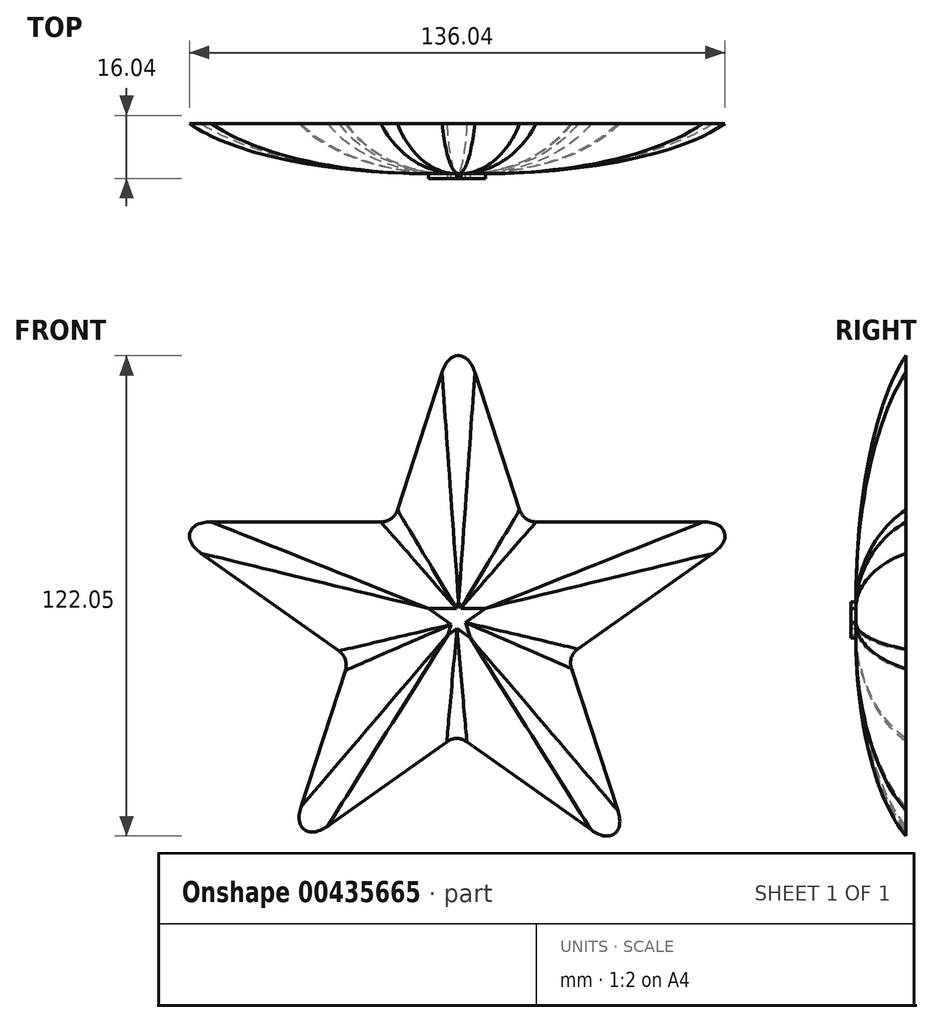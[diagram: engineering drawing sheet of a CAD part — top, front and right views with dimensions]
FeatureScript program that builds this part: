
annotation { "Feature Type Name" : "Feature", "Feature Type Description" : "" }
export const myFeature = defineFeature(function(context is Context, id is Id, definition is map)
    precondition{}
    {
        {
            var Q0;
            Q0=qCreatedBy(makeId("Front.planeOp"),FACE);
            var sketch = newSketch(context, id + "F0", { "sketchPlane" : qUnion([Q0])});
            skLineSegment(sketch, "E0", {"start": v(-44.05, -76) * mm, "end": v(76, 8.97) * mm});
            skLineSegment(sketch, "E1", {"start": v(76, 8.97) * mm, "end": v(-76.57, 8.97) * mm});
            skLineSegment(sketch, "E2", {"start": v(-76.57, 8.97) * mm, "end": v(43.16, -76) * mm});
            skLineSegment(sketch, "E3", {"start": v(44.3, -76) * mm, "end": v(0, 59.77) * mm});
            skLineSegment(sketch, "E4", {"start": v(0, 59.77) * mm, "end": v(-44.05, -76) * mm});
            skLineSegment(sketch, "E5", {"start": v(43.16, -76) * mm, "end": v(44.3, -76) * mm});
            skSolve(sketch);
        }
        {
            var Q0;
            {var subQ0=sQuery(id+"F0.wireOp",EDGE,"E3");var subQ1=sQuery(id+"F0.wireOp",EDGE,"E1");var subQ2=makeQuery(id+"F0.imprint","INTERSECT",VERTEX,{"derivedFrom":[subQ1,subQ0]});Q0=makeQuery(id+"F0.imprint","IMPRINT",FACE,{"disambiguationData":[TD([[makeQuery(id+"F0.imprint","IMPRINT",EDGE,{"disambiguationData":[TD([[subQ2,-1.0]])],"derivedFrom":subQ1}),-1.0]])]});}
            var Q1;
            {var subQ0=sQuery(id+"F0.wireOp",EDGE,"E2");var subQ1=sQuery(id+"F0.wireOp",EDGE,"E1");var subQ2=makeQuery(id+"F0.imprint","INTERSECT",VERTEX,{"derivedFrom":[subQ1,subQ0]});Q1=makeQuery(id+"F0.imprint","IMPRINT",FACE,{"disambiguationData":[TD([[makeQuery(id+"F0.imprint","IMPRINT",EDGE,{"disambiguationData":[TD([[subQ2,1.0]])],"derivedFrom":subQ1}),1.0]])]});}
            var Q2;
            {var subQ0=sQuery(id+"F0.wireOp",EDGE,"E4");var subQ1=sQuery(id+"F0.wireOp",EDGE,"E0");var subQ2=makeQuery(id+"F0.imprint","INTERSECT",VERTEX,{"derivedFrom":[subQ1,subQ0]});Q2=makeQuery(id+"F0.imprint","IMPRINT",FACE,{"disambiguationData":[TD([[makeQuery(id+"F0.imprint","IMPRINT",EDGE,{"disambiguationData":[TD([[subQ2,-1.0]])],"derivedFrom":subQ1}),1.0]])]});}
            var Q3;
            {var subQ0=sQuery(id+"F0.wireOp",EDGE,"E1");var subQ1=sQuery(id+"F0.wireOp",EDGE,"E0");var subQ2=makeQuery(id+"F0.imprint","INTERSECT",VERTEX,{"derivedFrom":[subQ1,subQ0]});Q3=makeQuery(id+"F0.imprint","IMPRINT",FACE,{"disambiguationData":[TD([[makeQuery(id+"F0.imprint","IMPRINT",EDGE,{"disambiguationData":[TD([[subQ2,1.0]])],"derivedFrom":subQ1}),1.0]])]});}
            var Q4;
            {var subQ5=sQuery(id+"F0.wireOp",EDGE,"E5");Q4=makeQuery(id+"F0.imprint","IMPRINT",FACE,{"disambiguationData":[TD([[makeQuery(id+"F0.imprint","IMPRINT",EDGE,{"derivedFrom":subQ5}),1.0]])]});}
            var Q5;
            {var subQ1=sQuery(id+"F0.wireOp",EDGE,"E0");var subQ5=sQuery(id+"F0.wireOp",EDGE,"E2");var subQ6=makeQuery(id+"F0.imprint","INTERSECT",VERTEX,{"derivedFrom":[subQ1,subQ5]});Q5=makeQuery(id+"F0.imprint","IMPRINT",FACE,{"disambiguationData":[TD([[makeQuery(id+"F0.imprint","IMPRINT",EDGE,{"disambiguationData":[TD([[subQ6,-1.0]])],"derivedFrom":subQ1}),1.0]])]});}
            extrude(context, id + "F1", {"entities" : qUnion([Q0, Q1, Q2, Q3, Q4, Q5]), "depth" : 12.7 * mm});
        }
        {
            var Q0;
            Q0=makeQuery(id+"F1.opExtrude","CAP_FACE",FACE,{"disambiguationData":[OSD([sQuery(id+"F0.wireOp",EDGE,"E0"),sQuery(id+"F0.wireOp",EDGE,"E1"),sQuery(id+"F0.wireOp",EDGE,"E2"),sQuery(id+"F0.wireOp",EDGE,"E3"),sQuery(id+"F0.wireOp",EDGE,"E4"),sQuery(id+"F0.wireOp",EDGE,"E5")])],"isStart":false});
            fillet(context, id + "F2", {"entities" : qUnion([Q0]), "radius" : 25.4 * mm, "tangentPropagation" : true, "allowEdgeOverflow" : false});
        }
        {
            var Q0;
            {var subQ0=sQuery(id+"F0.wireOp",EDGE,"E2");var subQ1=sQuery(id+"F0.wireOp",EDGE,"E1");var subQ2=makeQuery(id+"F0.imprint","INTERSECT",VERTEX,{"derivedFrom":[subQ1,subQ0]});Q0=makeQuery(id+"F2.opFillet","BLEND_EDGE",EDGE,{"blendedFrom":[makeQuery(id+"F1.opExtrude","CAP_EDGE",EDGE,{"disambiguationData":[OSD([subQ1]),TDD([makeQuery(id+"F0.imprint","IMPRINT",EDGE,{"disambiguationData":[TD([[subQ2,1.0]])],"derivedFrom":subQ1})])],"isStart":false}),makeQuery(id+"F1.opExtrude","CAP_EDGE",EDGE,{"disambiguationData":[OSD([subQ0]),TDD([makeQuery(id+"F0.imprint","IMPRINT",EDGE,{"disambiguationData":[TD([[subQ2,-1.0]])],"derivedFrom":subQ0})])],"isStart":false})],"blendedInto":[]});}
            fillet(context, id + "F3", {"entities" : qUnion([Q0]), "radius" : 5.08 * mm, "tangentPropagation" : true, "allowEdgeOverflow" : false});
        }
        {
            var Q0;
            {var subQ0=sQuery(id+"F0.wireOp",EDGE,"E4");var subQ1=sQuery(id+"F0.wireOp",EDGE,"E3");var subQ2=makeQuery(id+"F0.imprint","INTERSECT",VERTEX,{"derivedFrom":[subQ1,subQ0]});Q0=makeQuery(id+"F2.opFillet","BLEND_EDGE",EDGE,{"blendedFrom":[makeQuery(id+"F1.opExtrude","CAP_EDGE",EDGE,{"disambiguationData":[OSD([subQ1]),TDD([makeQuery(id+"F0.imprint","IMPRINT",EDGE,{"disambiguationData":[TD([[subQ2,1.0]])],"derivedFrom":subQ1})])],"isStart":false}),makeQuery(id+"F1.opExtrude","CAP_EDGE",EDGE,{"disambiguationData":[OSD([subQ0]),TDD([makeQuery(id+"F0.imprint","IMPRINT",EDGE,{"disambiguationData":[TD([[subQ2,-1.0]])],"derivedFrom":subQ0})])],"isStart":false})],"blendedInto":[]});}
            fillet(context, id + "F4", {"entities" : qUnion([Q0]), "radius" : 5.08 * mm, "tangentPropagation" : true, "allowEdgeOverflow" : false});
        }
        {
            var Q0;
            {var subQ0=sQuery(id+"F0.wireOp",EDGE,"E4");var subQ1=sQuery(id+"F0.wireOp",EDGE,"E0");var subQ2=makeQuery(id+"F0.imprint","INTERSECT",VERTEX,{"derivedFrom":[subQ1,subQ0]});Q0=makeQuery(id+"F2.opFillet","BLEND_EDGE",EDGE,{"blendedFrom":[makeQuery(id+"F1.opExtrude","CAP_EDGE",EDGE,{"disambiguationData":[OSD([subQ1]),TDD([makeQuery(id+"F0.imprint","IMPRINT",EDGE,{"disambiguationData":[TD([[subQ2,-1.0]])],"derivedFrom":subQ1})])],"isStart":false}),makeQuery(id+"F1.opExtrude","CAP_EDGE",EDGE,{"disambiguationData":[OSD([subQ0]),TDD([makeQuery(id+"F0.imprint","IMPRINT",EDGE,{"disambiguationData":[TD([[subQ2,1.0]])],"derivedFrom":subQ0})])],"isStart":false})],"blendedInto":[]});}
            fillet(context, id + "F5", {"entities" : qUnion([Q0]), "radius" : 5.08 * mm, "tangentPropagation" : true, "allowEdgeOverflow" : false});
        }
        {
            var Q0;
            {var subQ0=sQuery(id+"F0.wireOp",EDGE,"E5");var subQ1=sQuery(id+"F0.wireOp",EDGE,"E3");var subQ3=sQuery(id+"F0.wireOp",EDGE,"E2");Q0=makeQuery(id+"F2.opFillet","BLEND_EDGE",EDGE,{"blendedFrom":[makeQuery(id+"F1.opExtrude","CAP_EDGE",EDGE,{"disambiguationData":[OSD([subQ3]),TDD([makeQuery(id+"F0.imprint","IMPRINT",EDGE,{"disambiguationData":[TD([[makeQuery(id+"F0.imprint","INTERSECT",VERTEX,{"derivedFrom":[subQ3,subQ0]}),1.0]])],"derivedFrom":subQ3})])],"isStart":false}),makeQuery(id+"F1.opExtrude","CAP_EDGE",EDGE,{"disambiguationData":[OSD([subQ1]),TDD([makeQuery(id+"F0.imprint","IMPRINT",EDGE,{"disambiguationData":[TD([[makeQuery(id+"F0.imprint","INTERSECT",VERTEX,{"derivedFrom":[subQ1,subQ0]}),-1.0]])],"derivedFrom":subQ1})])],"isStart":false})],"blendedInto":[]});}
            fillet(context, id + "F6", {"entities" : qUnion([Q0]), "radius" : 5.08 * mm, "tangentPropagation" : true, "allowEdgeOverflow" : false});
        }
        {
            var Q0;
            {var subQ0=sQuery(id+"F0.wireOp",EDGE,"E1");var subQ1=sQuery(id+"F0.wireOp",EDGE,"E0");var subQ2=makeQuery(id+"F0.imprint","INTERSECT",VERTEX,{"derivedFrom":[subQ1,subQ0]});Q0=makeQuery(id+"F2.opFillet","BLEND_EDGE",EDGE,{"blendedFrom":[makeQuery(id+"F1.opExtrude","CAP_EDGE",EDGE,{"disambiguationData":[OSD([subQ1]),TDD([makeQuery(id+"F0.imprint","IMPRINT",EDGE,{"disambiguationData":[TD([[subQ2,1.0]])],"derivedFrom":subQ1})])],"isStart":false}),makeQuery(id+"F1.opExtrude","CAP_EDGE",EDGE,{"disambiguationData":[OSD([subQ0]),TDD([makeQuery(id+"F0.imprint","IMPRINT",EDGE,{"disambiguationData":[TD([[subQ2,-1.0]])],"derivedFrom":subQ0})])],"isStart":false})],"blendedInto":[]});}
            fillet(context, id + "F7", {"entities" : qUnion([Q0]), "radius" : 5.08 * mm, "tangentPropagation" : true, "allowEdgeOverflow" : false});
        }
        {
            var Q0;
            {var subQ0=sQuery(id+"F0.wireOp",EDGE,"E3");var subQ1=sQuery(id+"F0.wireOp",EDGE,"E1");Q0=makeQuery(id+"F2.opFillet","BLEND_EDGE",EDGE,{"blendedFrom":[makeQuery(id+"F1.opExtrude","CAP_EDGE",EDGE,{"disambiguationData":[OSD([subQ1]),TDD([makeQuery(id+"F0.imprint","IMPRINT",EDGE,{"disambiguationData":[TD([[makeQuery(id+"F0.imprint","INTERSECT",VERTEX,{"derivedFrom":[sQuery(id+"F0.wireOp",EDGE,"E0"),subQ1]}),-1.0]])],"derivedFrom":subQ1})])],"isStart":false}),makeQuery(id+"F1.opExtrude","CAP_EDGE",EDGE,{"disambiguationData":[OSD([subQ0]),TDD([makeQuery(id+"F0.imprint","IMPRINT",EDGE,{"disambiguationData":[TD([[makeQuery(id+"F0.imprint","INTERSECT",VERTEX,{"derivedFrom":[subQ0,sQuery(id+"F0.wireOp",EDGE,"E4")]}),1.0]])],"derivedFrom":subQ0})])],"isStart":false})],"blendedInto":[]});}
            fillet(context, id + "F8", {"entities" : qUnion([Q0]), "radius" : 5.08 * mm, "tangentPropagation" : true, "allowEdgeOverflow" : false});
        }
        {
            var Q0;
            {var subQ0=sQuery(id+"F0.wireOp",EDGE,"E4");var subQ1=sQuery(id+"F0.wireOp",EDGE,"E1");Q0=makeQuery(id+"F2.opFillet","BLEND_EDGE",EDGE,{"blendedFrom":[makeQuery(id+"F1.opExtrude","CAP_EDGE",EDGE,{"disambiguationData":[OSD([subQ1]),TDD([makeQuery(id+"F0.imprint","IMPRINT",EDGE,{"disambiguationData":[TD([[makeQuery(id+"F0.imprint","INTERSECT",VERTEX,{"derivedFrom":[subQ1,sQuery(id+"F0.wireOp",EDGE,"E2")]}),1.0]])],"derivedFrom":subQ1})])],"isStart":false}),makeQuery(id+"F1.opExtrude","CAP_EDGE",EDGE,{"disambiguationData":[OSD([subQ0]),TDD([makeQuery(id+"F0.imprint","IMPRINT",EDGE,{"disambiguationData":[TD([[makeQuery(id+"F0.imprint","INTERSECT",VERTEX,{"derivedFrom":[sQuery(id+"F0.wireOp",EDGE,"E3"),subQ0]}),-1.0]])],"derivedFrom":subQ0})])],"isStart":false})],"blendedInto":[]});}
            var Q1;
            {var subQ0=sQuery(id+"F0.wireOp",EDGE,"E4");var subQ1=sQuery(id+"F0.wireOp",EDGE,"E2");Q1=makeQuery(id+"F2.opFillet","BLEND_EDGE",EDGE,{"blendedFrom":[makeQuery(id+"F1.opExtrude","CAP_EDGE",EDGE,{"disambiguationData":[OSD([subQ1]),TDD([makeQuery(id+"F0.imprint","IMPRINT",EDGE,{"disambiguationData":[TD([[makeQuery(id+"F0.imprint","INTERSECT",VERTEX,{"derivedFrom":[sQuery(id+"F0.wireOp",EDGE,"E1"),subQ1]}),-1.0]])],"derivedFrom":subQ1})])],"isStart":false}),makeQuery(id+"F1.opExtrude","CAP_EDGE",EDGE,{"disambiguationData":[OSD([subQ0]),TDD([makeQuery(id+"F0.imprint","IMPRINT",EDGE,{"disambiguationData":[TD([[makeQuery(id+"F0.imprint","INTERSECT",VERTEX,{"derivedFrom":[sQuery(id+"F0.wireOp",EDGE,"E0"),subQ0]}),1.0]])],"derivedFrom":subQ0})])],"isStart":false})],"blendedInto":[]});}
            var Q2;
            {var subQ0=sQuery(id+"F0.wireOp",EDGE,"E2");var subQ1=sQuery(id+"F0.wireOp",EDGE,"E0");Q2=makeQuery(id+"F2.opFillet","BLEND_EDGE",EDGE,{"blendedFrom":[makeQuery(id+"F1.opExtrude","CAP_EDGE",EDGE,{"disambiguationData":[OSD([subQ1]),TDD([makeQuery(id+"F0.imprint","IMPRINT",EDGE,{"disambiguationData":[TD([[makeQuery(id+"F0.imprint","INTERSECT",VERTEX,{"derivedFrom":[subQ1,sQuery(id+"F0.wireOp",EDGE,"E4")]}),-1.0]])],"derivedFrom":subQ1})])],"isStart":false}),makeQuery(id+"F1.opExtrude","CAP_EDGE",EDGE,{"disambiguationData":[OSD([subQ0]),TDD([makeQuery(id+"F0.imprint","IMPRINT",EDGE,{"disambiguationData":[TD([[makeQuery(id+"F0.imprint","INTERSECT",VERTEX,{"derivedFrom":[subQ0,sQuery(id+"F0.wireOp",EDGE,"E5")]}),1.0]])],"derivedFrom":subQ0})])],"isStart":false})],"blendedInto":[]});}
            var Q3;
            {var subQ0=sQuery(id+"F0.wireOp",EDGE,"E3");var subQ1=sQuery(id+"F0.wireOp",EDGE,"E0");Q3=makeQuery(id+"F2.opFillet","BLEND_EDGE",EDGE,{"blendedFrom":[makeQuery(id+"F1.opExtrude","CAP_EDGE",EDGE,{"disambiguationData":[OSD([subQ1]),TDD([makeQuery(id+"F0.imprint","IMPRINT",EDGE,{"disambiguationData":[TD([[makeQuery(id+"F0.imprint","INTERSECT",VERTEX,{"derivedFrom":[subQ1,sQuery(id+"F0.wireOp",EDGE,"E1")]}),1.0]])],"derivedFrom":subQ1})])],"isStart":false}),makeQuery(id+"F1.opExtrude","CAP_EDGE",EDGE,{"disambiguationData":[OSD([subQ0]),TDD([makeQuery(id+"F0.imprint","IMPRINT",EDGE,{"disambiguationData":[TD([[makeQuery(id+"F0.imprint","INTERSECT",VERTEX,{"derivedFrom":[subQ0,sQuery(id+"F0.wireOp",EDGE,"E5")]}),-1.0]])],"derivedFrom":subQ0})])],"isStart":false})],"blendedInto":[]});}
            fillet(context, id + "F9", {"entities" : qUnion([Q0, Q1, Q2, Q3]), "radius" : 5.08 * mm, "tangentPropagation" : true, "allowEdgeOverflow" : false});
        }
        {
            var Q0;
            Q0=makeQuery(id+"F1.opExtrude","CAP_FACE",FACE,{"disambiguationData":[OSD([sQuery(id+"F0.wireOp",EDGE,"E0"),sQuery(id+"F0.wireOp",EDGE,"E1"),sQuery(id+"F0.wireOp",EDGE,"E2"),sQuery(id+"F0.wireOp",EDGE,"E3"),sQuery(id+"F0.wireOp",EDGE,"E4"),sQuery(id+"F0.wireOp",EDGE,"E5")])],"isStart":false});
            extrude(context, id + "F10", {"entities" : qUnion([Q0]), "operationType" : NewBodyOperationType.ADD, "depth" : 1.27 * mm, "offsetDistance" : 25.4 * mm});
        }
    });
